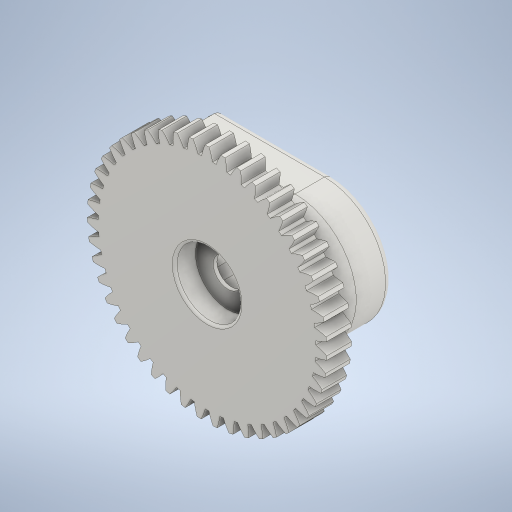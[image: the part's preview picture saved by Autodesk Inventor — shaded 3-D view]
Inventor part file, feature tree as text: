
AUTODESK INVENTOR PART (.ipt)
format: ipt  version: 2024.1 (Build 281209000, 209)  size: 830,976 bytes
history: native  units: mm (DEFAULTED — no unit token found)
features: sketch x10, extrude x9, fillet x4, plane x3, other x3
ambient origin geometry x8: Origin, YZ Plane, XZ Plane, XY Plane, X Axis, Y Axis, Z Axis, Center Point
bodies: Solid1 (feature_tree)
feature tree (29):
  extrude  "Extrusion1"  Depth=10.0mm TaperAngle=0.0deg
  plane  "Work Plane2"
  plane  "Work Plane8"
  plane  "Work Plane9"
  other  "Engrenagem reta"
  extrude  "Extrusão2"  Depth=10.0mm TaperAngle=0.0deg
  sketch  "Esboço4"  dims[d16=70.0mm d17=0.0mm d34=0.668424mm d39=0.0mm d41=0.0mm]
  extrude  "Extrusão3"  Depth=0.668424mm TaperAngle=0.0deg
  fillet  "Arredondamento3"  [1 undecoded]
  fillet  "Arredondamento4"  [1 undecoded]
  extrude  "Extrusão4"  Depth=70.0mm
  extrude  "Extrusão5"  Depth=2.0mm
  extrude  "Extrusão6"  Depth=10.0mm
  extrude  "Extrusão7"  Depth=22.0mm
  fillet  "Arredondamento8"  Radius=22.0mm
  extrude  "Extrusão8"  Depth=9.0mm
  fillet  "Arredondamento9"  Radius=11.0mm
  extrude  "Extrusão9"  Depth=18.0mm
  sketch  "Sketch1"  dims[d0=98.0mm d1=10.0mm d2=0.0mm]
  other  "Srf1"
  sketch  "Esboço3"  dims[d3=94.0mm d4=10.0mm d5=0.0mm]
  sketch  "Esboço5"  dims[d43=70.0mm d46=70.0mm]
  sketch  "Esboço6"  dims[d47=0.0mm d48=0.0mm d50=2.0mm]
  sketch  "Esboço7"  dims[d51=10.0mm d52=0.0mm d60=7.0mm]
  sketch  "Esboço8"  dims[d61=14.0mm d62=11.0mm d63=22.0mm]
  sketch  "Esboço9"  dims[d64=9.0mm d65=20.0mm d66=11.0mm]
  sketch  "Esboço10"  dims[d67=23.0mm d68=18.0mm]
  sketch  "Esboço11"  dims[d69=18.0mm d70=9.0mm d71=9.0mm d72=25.0mm d73=25.0mm d74=25.0mm d75=30.0mm d76=0.0mm d79=15.0mm d80=0.5mm d83=7.0mm d84=11.0mm d85=22.0mm d86=6.0mm d87=0.3mm d88=32.2mm d89=6.0mm d90=0.3mm d91=14.3mm d92=10.0mm d93=0.0mm d94=10.0mm d95=0.0mm d98=4.0mm d99=20.0mm d100=0.0mm d101=2.0mm d102=1.0mm d103=1.0mm d104=15.3mm d105=1.0mm d106=1.0mm d107=6.0mm d108=20.0mm d109=0.0mm d110=3.0mm d111=26.5mm d112=8.5mm d113=0.0mm d114=1.0mm d115=12.0mm d116=8.5mm d117=0.0mm]
  other  "Diâmetro do flanco"
note: 2 required parameter values undecoded (feature->parameter linkage not recoverable at this tier; creation-order binding heuristic only, values carry confidence <= 0.55)
